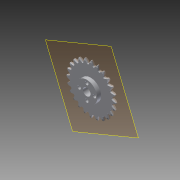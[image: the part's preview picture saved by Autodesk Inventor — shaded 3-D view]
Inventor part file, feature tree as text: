
AUTODESK INVENTOR PART (.ipt)
format: ipt  version: 2013 (Build 170138000, 138)  size: 798,208 bytes
history: native  units: in
note: dims shown in document units (in); Inventor stores cm internally (conversion verified against a paired STEP export)
features: imported_body x1, plane x1
ambient origin geometry x8: Origin, YZ Plane, XZ Plane, XY Plane, X Axis, Y Axis, Z Axis, Center Point
bodies: Solid1 (feature_tree)
feature tree (2):
  imported_body  "Base1"
  plane  "Work Plane1"
